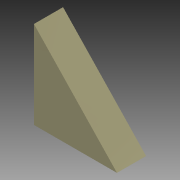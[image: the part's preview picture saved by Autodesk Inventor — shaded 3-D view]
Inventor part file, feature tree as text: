
AUTODESK INVENTOR PART (.ipt)
format: ipt  version: 2013 (Build 170138000, 138)  size: 68,608 bytes
history: native  units: in
note: dims shown in document units (in); Inventor stores cm internally (conversion verified against a paired STEP export)
features: extrude x1, sketch x1
ambient origin geometry x8: Origin, YZ Plane, XZ Plane, XY Plane, X Axis, Y Axis, Z Axis, Center Point
bodies: Solid1 (feature_tree)
feature tree (2):
  extrude  "Extrusion1"  Depth=3.0in
  sketch  "Sketch1"  dims[d0=2.85in d1=3.0in d2=90.0deg d3=1.0in d4=0.0in]
